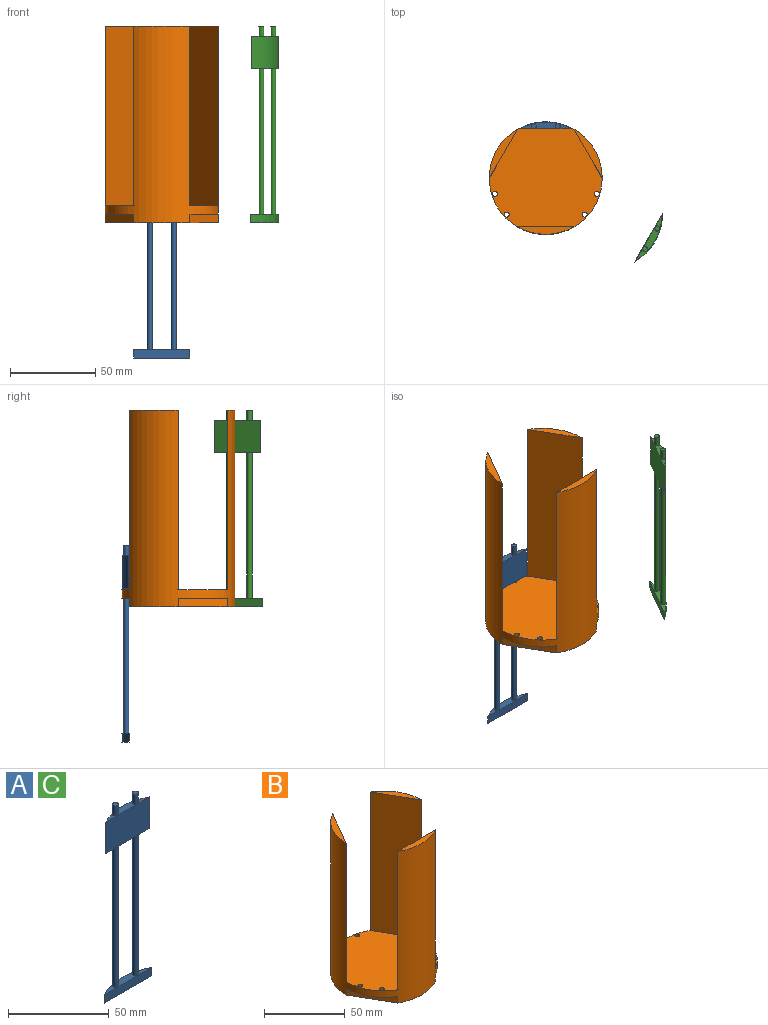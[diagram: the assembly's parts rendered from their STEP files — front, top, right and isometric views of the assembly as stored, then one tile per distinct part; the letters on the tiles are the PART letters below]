
ASSEMBLY  parts=3 mates=1
PART A: 14 faces, bbox 33x4.4x115 mm
  f0: cylinder r=1.5mm len=85mm, axis (0,0,-1), area 801.1mm2, adj f4,f9
  f1: cylinder r=1.5mm len=85mm, axis (0,0,-1), area 801.1mm2, adj f4,f9
  f2: cylinder r=33mm len=33mm, axis (0,0,-1), area 172.8mm2, adj f3,f4,f5
  f3: plane 33x5mm, normal (0,-1,0), area 165mm2, adj f2,f4,f5
  f4: plane 33x4.42mm, normal (0,0,1), area 84.5mm2, adj f0,f1,f2,f3
  f5: plane 33x4.42mm, normal (0,0,-1), area 98.6mm2, adj f2,f3
  f6: plane 31x19mm, normal (0,-1,0), area 589mm2, adj f7,f8,f9
  f7: cylinder r=32mm len=31mm, axis (0,0,-1), area 614.9mm2, adj f6,f8,f9
  f8: plane 31x4mm, normal (0,0,1), area 69.7mm2, adj f6,f7,f11,f13
  f9: plane 31x4mm, normal (0,0,-1), area 69.7mm2, adj f0,f1,f6,f7
  f10: plane 3x3mm, normal (0,0,1), area 7.1mm2, adj f11
  f11: cylinder r=1.5mm len=6mm, axis (0,0,-1), area 56.5mm2, adj f8,f10
  f12: plane 3x3mm, normal (0,0,1), area 7.1mm2, adj f13
  f13: cylinder r=1.5mm len=6mm, axis (0,0,-1), area 56.5mm2, adj f8,f12
PART B: 21 faces, bbox 66x66x115 mm
  f0: plane 28.58x16.5mm, normal (0.87,-0.5,0), area 165mm2, adj f4,f6,f20
  f1: plane 28.58x16.5mm, normal (-0.87,-0.5,0), area 165mm2, adj f4,f6,f17
  f2: plane 33x5mm, normal (0,1,0), area 165mm2, adj f4,f6,f14
  f3: plane 66x61.58mm, normal (0,0,1), area 3082.8mm2, adj f5,f6,f8,f10,f12,f13,f15,f16
  f4: plane 66x61.58mm, normal (0,0,-1), area 3125.2mm2, adj f0,f1,f2,f6
  f5: plane 105x28.58mm, normal (-0.87,-0.5,0), area 3465mm2, adj f3,f6,f7
  f6: cylinder r=33mm len=115mm, axis (0,0,-1), area 12440.7mm2, adj f0,f1,f2,f3,f4,f5,f7,f8
  f7: plane 28.58x16.5mm, normal (0,0,1), area 98.6mm2, adj f5,f6
  f8: plane 105x28.58mm, normal (0.87,-0.5,0), area 3465mm2, adj f3,f6,f9
  f9: plane 28.58x16.5mm, normal (0,0,1), area 98.6mm2, adj f6,f8
  f10: plane 105x33mm, normal (0,1,0), area 3465mm2, adj f3,f6,f11
  f11: plane 33x4.42mm, normal (0,0,1), area 98.6mm2, adj f6,f10
  f12: cylinder r=1.5mm len=5mm, axis (0,0,-1), area 47.1mm2, adj f3,f14
  f13: cylinder r=1.5mm len=5mm, axis (0,0,-1), area 47.1mm2, adj f3,f14
  f14: plane 33x4.42mm, normal (0,0,-1), area 84.5mm2, adj f2,f6,f12,f13
  f15: cylinder r=1.5mm len=5mm, axis (0,0,-1), area 47.1mm2, adj f3,f17
  f16: cylinder r=1.5mm len=5mm, axis (0,0,-1), area 47.1mm2, adj f3,f17
  f17: plane 28.58x16.5mm, normal (0,0,-1), area 84.5mm2, adj f1,f6,f15,f16
  f18: cylinder r=1.5mm len=5mm, axis (0,0,-1), area 47.1mm2, adj f3,f20
  f19: cylinder r=1.5mm len=5mm, axis (0,0,-1), area 47.1mm2, adj f3,f20
  f20: plane 28.58x16.5mm, normal (0,0,-1), area 84.5mm2, adj f0,f6,f18,f19
PART C: same geometry as A
PLACE A t=(-40.78,0.3,-100.94)mm
PLACE B t=(-40.78,0.3,-21.74)mm fixed
PLACE C rot(axis=(0,0,-1),120deg) t=(-5.36,-20.15,-21.74)mm
MATE slider B.f13 <-> A.f1  axis (0,0,-1) through (-33.78,30.68,-16.74)mm
